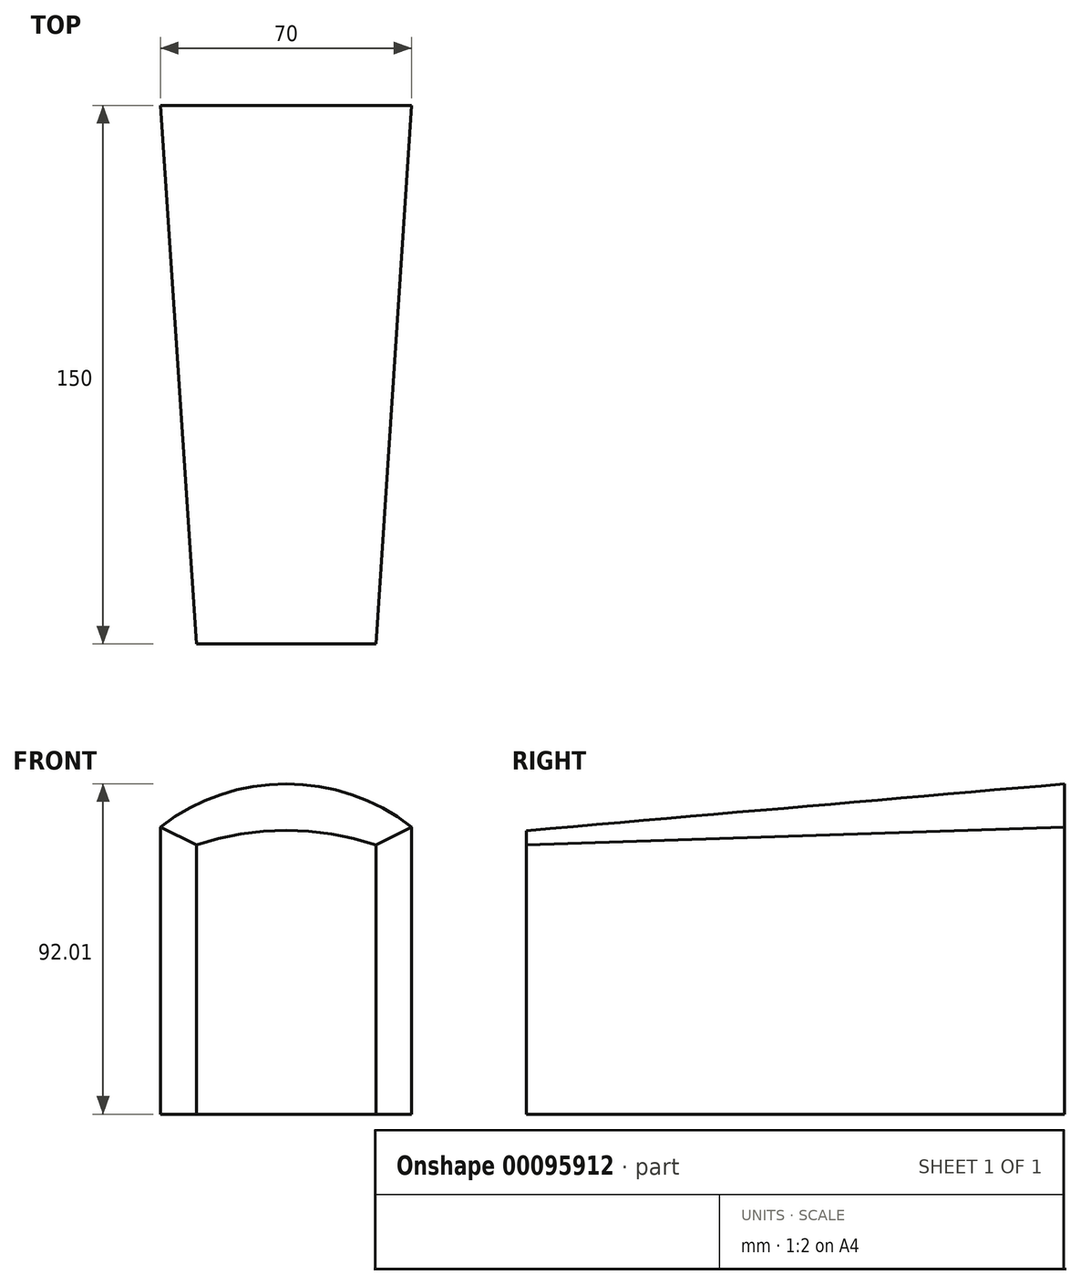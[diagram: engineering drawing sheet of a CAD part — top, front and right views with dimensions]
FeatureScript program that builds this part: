
annotation { "Feature Type Name" : "Feature", "Feature Type Description" : "" }
export const myFeature = defineFeature(function(context is Context, id is Id, definition is map)
    precondition{}
    {
        {
            var Q0;
            Q0=qCreatedBy(makeId("Front.planeOp"),FACE);
            var sketch = newSketch(context, id + "F0", { "sketchPlane" : qUnion([Q0])});
            skLineSegment(sketch, "E0.bottom", {"start": v(-35, 40) * mm, "end": v(35, 40) * mm});
            skLineSegment(sketch, "E0.top", {"start": v(-35, -40) * mm, "end": v(35, -40) * mm});
            skLineSegment(sketch, "E0.left", {"start": v(-35, 40) * mm, "end": v(-35, -40) * mm});
            skLineSegment(sketch, "E0.right", {"start": v(35, 40) * mm, "end": v(35, -40) * mm});
            skArc(sketch, "E1", {"start": v(35, 40) * mm, "mid": v(0, 52.01) * mm, "end": v(-35, 40) * mm});
            skSolve(sketch);
        }
        {
            var Q0;
            Q0=qCreatedBy(makeId("Front.planeOp"),FACE);
            cPlane(context, id + "F1", {"entities" : qUnion([Q0]), "cplaneType" : CPlaneType.OFFSET, "offset" : 150 * mm, "width" : 150 * mm, "height" : 150 * mm});
        }
        {
            var Q0;
            Q0=qCreatedBy(id+"F1.planeOp",FACE);
            var sketch = newSketch(context, id + "F2", { "sketchPlane" : qUnion([Q0])});
            skLineSegment(sketch, "E2.bottom", {"start": v(-25, 35) * mm, "end": v(25, 35) * mm});
            skLineSegment(sketch, "E2.top", {"start": v(-25, -40) * mm, "end": v(25, -40) * mm});
            skLineSegment(sketch, "E2.left", {"start": v(-25, 35) * mm, "end": v(-25, -40) * mm});
            skLineSegment(sketch, "E2.right", {"start": v(25, 35) * mm, "end": v(25, -40) * mm});
            skArc(sketch, "E3", {"start": v(25, 35) * mm, "mid": v(0, 39) * mm, "end": v(-25, 35) * mm});
            skSolve(sketch);
        }
        {
            var Q0;
            Q0 = qSketchRegion(id + "F0", true);
            var Q1;
            Q1 = qSketchRegion(id + "F2", true);
            loft(context, id + "F3", {"sheetProfilesArray" : [{ "sheetProfileEntities" : qUnion([Q0]) }, { "sheetProfileEntities" : qUnion([Q1]) }]});
        }
    });
